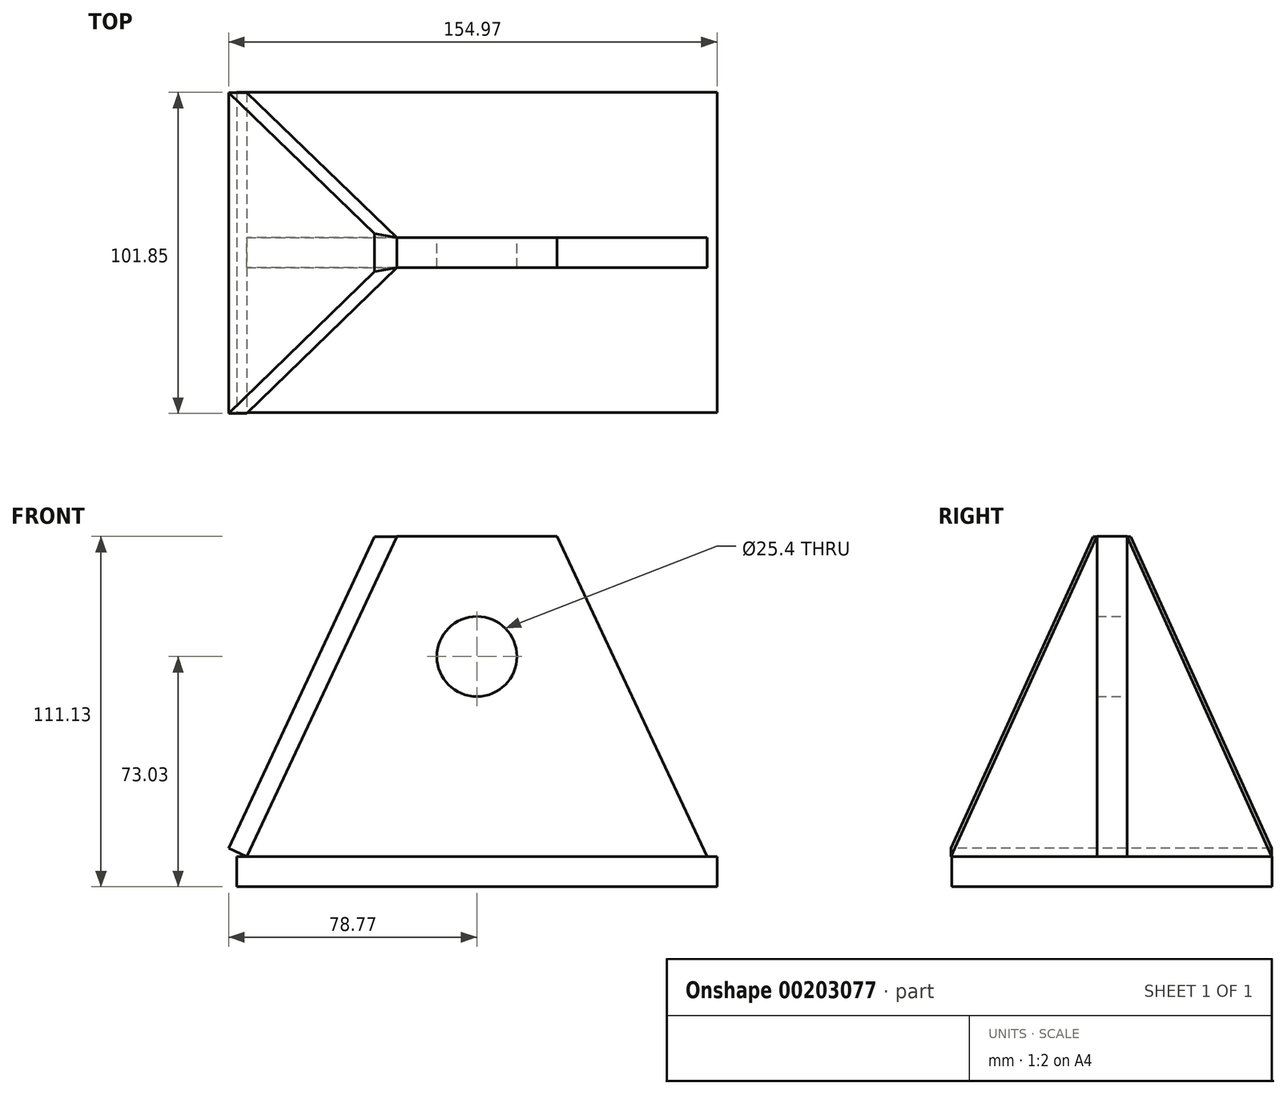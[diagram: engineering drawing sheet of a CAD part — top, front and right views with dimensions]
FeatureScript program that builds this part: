
annotation { "Feature Type Name" : "Feature", "Feature Type Description" : "" }
export const myFeature = defineFeature(function(context is Context, id is Id, definition is map)
    precondition{}
    {
        {
            var Q0;
            Q0=qCreatedBy(makeId("Front.planeOp"),FACE);
            var sketch = newSketch(context, id + "F0", { "sketchPlane" : qUnion([Q0])});
            skLineSegment(sketch, "E0", {"start": v(-73.03, 0) * mm, "end": v(73.03, 0) * mm});
            skLineSegment(sketch, "E1", {"start": v(25.4, 101.6) * mm, "end": v(-25.4, 101.6) * mm});
            skLineSegment(sketch, "E2", {"start": v(-25.4, 101.6) * mm, "end": v(-73.03, 0) * mm});
            skLineSegment(sketch, "E3", {"start": v(25.4, 101.6) * mm, "end": v(73.03, 0) * mm});
            skCircle(sketch, "E4", {"center": v(0, 63.5) * mm, "radius": 12.7 * mm});
            skSolve(sketch);
        }
        {
            var Q0;
            Q0 = qSketchRegion(id + "F0", true);
            extrude(context, id + "F1", {"entities" : qUnion([Q0]), "endBound" : BoundingType.SYMMETRIC, "depth" : 9.52 * mm});
        }
        {
            var Q0;
            Q0=makeQuery(id+"F1.opExtrude","SWEPT_FACE",FACE,{"disambiguationData":[OSD([sQuery(id+"F0.wireOp",EDGE,"E0")])]});
            var sketch = newSketch(context, id + "F2", { "sketchPlane" : qUnion([Q0])});
            skLineSegment(sketch, "E5.bottom", {"start": v(76.2, -50.8) * mm, "end": v(-76.2, -50.8) * mm});
            skLineSegment(sketch, "E5.top", {"start": v(76.2, 50.8) * mm, "end": v(-76.2, 50.8) * mm});
            skLineSegment(sketch, "E5.left", {"start": v(76.2, -50.8) * mm, "end": v(76.2, 50.8) * mm});
            skLineSegment(sketch, "E5.right", {"start": v(-76.2, -50.8) * mm, "end": v(-76.2, 50.8) * mm});
            skPoint(sketch, "E5.middle", {"position": v(0, 0) * mm});
            skSolve(sketch);
        }
        {
            var Q0;
            Q0 = qSketchRegion(id + "F2", true);
            extrude(context, id + "F3", {"entities" : qUnion([Q0]), "depth" : 9.52 * mm});
        }
        {
            var Q0;
            Q0=makeQuery(id+"F1.opExtrude","SWEPT_FACE",FACE,{"disambiguationData":[OSD([sQuery(id+"F0.wireOp",EDGE,"E2")])]});
            var sketch = newSketch(context, id + "F4", { "sketchPlane" : qUnion([Q0])});
            skLineSegment(sketch, "E6", {"start": v(-4.76, 81.21) * mm, "end": v(-50.66, -31) * mm});
            skLineSegment(sketch, "E7", {"start": v(-50.66, -31) * mm, "end": v(51.05, -31) * mm});
            skLineSegment(sketch, "E8", {"start": v(51.05, -31) * mm, "end": v(4.76, 81.21) * mm});
            skLineSegment(sketch, "E9", {"start": v(4.76, 81.21) * mm, "end": v(-4.76, 81.21) * mm});
            skSolve(sketch);
        }
        {
            var Q0;
            Q0 = qSketchRegion(id + "F4", true);
            extrude(context, id + "F5", {"entities" : qUnion([Q0]), "depth" : 6.35 * mm});
        }
        {
            var Q0;
            Q0=makeQuery(id+"F5.opExtrude","CAP_EDGE",EDGE,{"disambiguationData":[OSD([sQuery(id+"F4.wireOp",EDGE,"E9")])],"isStart":false});
            chamfer(context, id + "F6", {"entities" : qUnion([Q0]), "chamferType" : ChamferType.OFFSET_ANGLE, "width" : 3.05 * mm, "oppositeDirection" : false, "angle" : 65 * degree, "tangentPropagation" : true});
        }
    });
